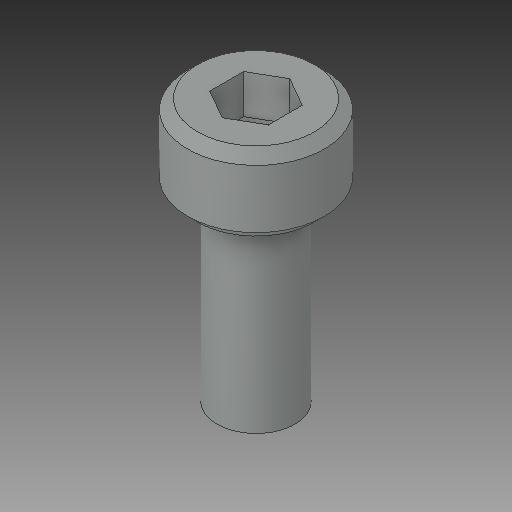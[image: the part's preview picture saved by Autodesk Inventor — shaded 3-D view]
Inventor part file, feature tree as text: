
AUTODESK INVENTOR PART (.ipt)
format: ipt  version: 2018 (Build 220112000, 112)  size: 107,008 bytes
history: native  units: in
note: dims shown in document units (in); Inventor stores cm internally (conversion verified against a paired STEP export)
features: chamfer x1
ambient origin geometry x8: Origin, YZ Plane, XZ Plane, XY Plane, X Axis, Y Axis, Z Axis, Center Point
bodies: Solid1 (feature_tree)
feature tree (1):
  chamfer  "Chamfer2"  [1 undecoded]
note: 1 required parameter value undecoded (feature->parameter linkage not recoverable at this tier; creation-order binding heuristic only, values carry confidence <= 0.55)
